# Revit family: Accessory-Desk_Mounted-Teknion-ZNDST_Table_Top_Screen-R2015
name_source: partatom
category: Furniture
revit_build: Autodesk Revit Architecture 2015 (Build: 20140323_1530(x64)
units: mm (PartAtom-declared; Revit-internal decimal feet)

## types (2) — shared parameters
Assembly Code = E2020200
Default Elevation = 48 "
Manufacturer = Teknion
Manufacturer Fax = 416.661.4586
Part Number = ZNDST
Product Documentation Link = http://www.teknion.com
Product Line = Zones
Product Page URL = http://www.teknion.com
Series = Zones
Sustainability Data = http://www.teknion.com
URL = www.teknion.com
Unit Weight URL = http://www.teknion.com
Warranty = http://www.teknion.com

## per-type parameters (varying)
| type | Description | Inner Width | Model | Screen Finish Note | Screen Upholstery | Width |
| 30" Width | Table Top Screen, 47" h x 30" w | 27 " | ZNDST4730 | Select a 30 inch material. | Mesh-StudioTK-K440-Knit Linx-Cool Grey (30" Width) | 30 " |
| 40" Width | Table Top Screen, 47" h x 40" w | 37 " | ZNDST4740 | Select a 40 inch material. | Mesh-StudioTK-K440-Knit Linx-Cool Grey (40" Width) | 40 " |

## geometry (parser evidence)
native form markers: Revolve x1, Sweep x2
no freeform markers — native parametric forms only
